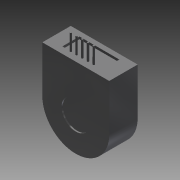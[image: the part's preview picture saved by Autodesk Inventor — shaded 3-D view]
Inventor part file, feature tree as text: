
AUTODESK INVENTOR PART (.ipt)
format: ipt  version: 2012 (Build 160160000, 160)  size: 112,640 bytes
history: native  units: in
note: dims shown in document units (in); Inventor stores cm internally (conversion verified against a paired STEP export)
features: extrude x4, sketch x2
ambient origin geometry x8: Origin, YZ Plane, XZ Plane, XY Plane, X Axis, Y Axis, Z Axis, Center Point
feature tree (6):
  sketch  "Sketch1"  dims[d0=1.175in d2=0.368in]
  extrude  "Extrusion2"  Depth=0.368in
  extrude  "Extrusion3"  Depth=0.5in
  sketch  "Sketch2"  dims[d3=0.25in d6=0.5in d7=0.5in d8=0.0in d9=0.024in d10=0.0in d11=0.7in d12=0.35in d13=0.3in d14=0.115in d15=0.03in d16=0.3875in d17=1.9685in d19=0.1in d20=0.3937in d22=1.0in d24=1.4in d25=0.3875in d26=0.042in d27=0.0in d28=0.288in d29=0.0in]
  extrude  "Extrusion4"  Depth=0.5in TaperAngle=0.0deg
  extrude  "Extrusion5"  Depth=0.024in TaperAngle=0.0deg
